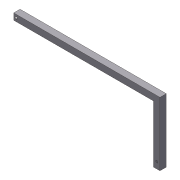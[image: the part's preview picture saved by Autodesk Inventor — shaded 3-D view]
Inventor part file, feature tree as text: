
AUTODESK INVENTOR PART (.ipt)
format: ipt  version: 2012 (Build 160160000, 160)  size: 93,184 bytes
history: native  units: in
note: dims shown in document units (in); Inventor stores cm internally (conversion verified against a paired STEP export)
features: extrude x3, sketch x3, shell x1
ambient origin geometry x8: Origin, YZ Plane, XZ Plane, XY Plane, X Axis, Y Axis, Z Axis, Center Point
bodies: Solid1 (feature_tree)
feature tree (7):
  extrude  "Extrusion1"  Depth=10.0in
  shell  "Shell1"  Thickness=10.0in
  extrude  "Extrusion2"  Depth=0.0625in
  extrude  "Extrusion3"  Depth=0.5in
  sketch  "Sketch1"  dims[d0=1.0in d1=10.0in d2=10.0in]
  sketch  "Sketch2"  dims[d3=1.0in d4=0.0in d5=0.0625in]
  sketch  "Sketch3"  dims[d6=0.375in d7=0.5in d8=1.0in d9=1.0in d10=0.0in d11=0.375in d12=0.5in d13=0.375in d14=1.0in d15=0.0in]
